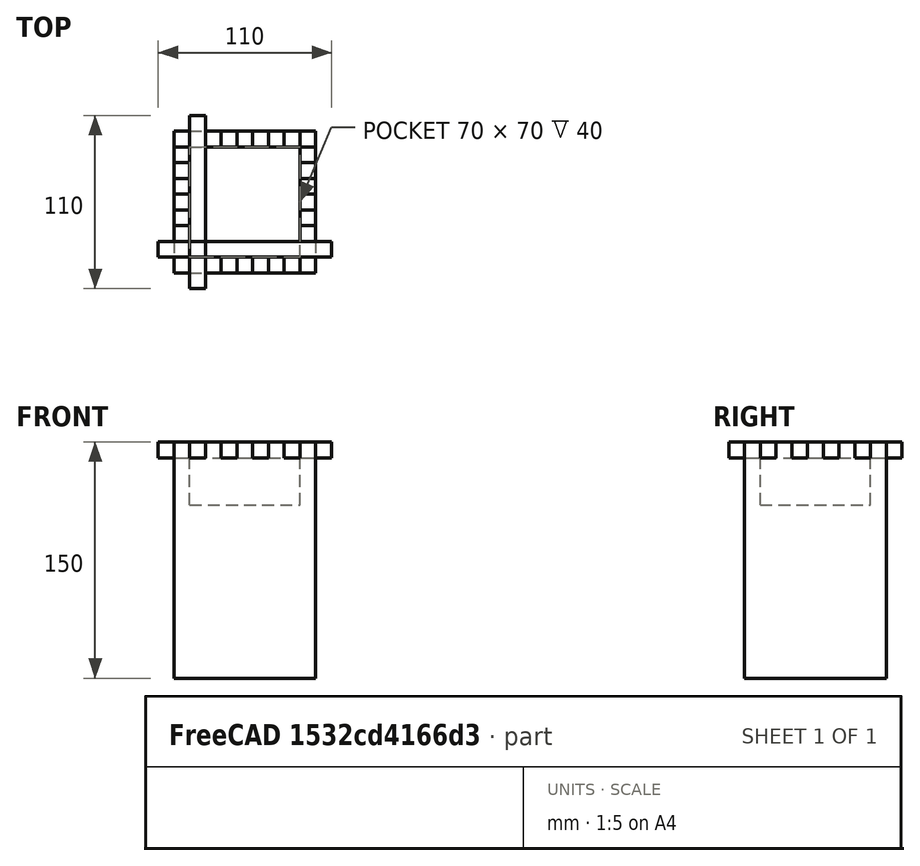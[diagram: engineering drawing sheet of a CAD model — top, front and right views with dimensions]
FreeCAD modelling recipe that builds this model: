
FCSTD DOCUMENT  (FreeCAD 0.21R33694 (Git))
Label: OJT1_T10_R03Castell
License: All rights reserved
LicenseURL: https://en.wikipedia.org/wiki/All_rights_reserved
objects: Part::Box×4, Part::Cut×3, Part::FeaturePython×2, Part::Refine×1
note: 8 computed .brp shape members not serialized (recipe doc carries the construction recipe); baked Part::Feature solids carry a one-line shape summary decoded from their .brp

FEATURE [Part::Box] Box  label="Cub"
  AttacherType = Attacher::AttachEngine3D
  Height = 10
  Length = 10
  Width = 110
FEATURE [Part::FeaturePython] Array  # Draft array (typed FeaturePython)
  AlwaysSyncPlacement = false
  Angle = 360
  ArrayType = 0
  Axis = (0,0,1)
  Base = -> Box
  Center = (0,0,0)
  Count = 4
  ExpandArray = false
  Fuse = false
  IntervalAxis = (0,0,0)
  IntervalX = (20,0,0)
  IntervalY = (0,100,0)
  IntervalZ = (0,0,100)
  NumberCircles = 3
  NumberPolar = 5
  NumberX = 4
  NumberY = 0
  NumberZ = 0
  PlacementList = 4 placements: arithmetic series from (0,0,0) step (20,0,0) to (60,0,0)
  RadialDistance = 50
  ScaleList = (4) [(1,1,1),(1,1,1),(1,1,1),(1,1,1)]
  Symmetry = 1
  TangentialDistance = 25
FEATURE [Part::Box] Box001  label="Cub001"
  AttacherType = Attacher::AttachEngine3D
  Height = 10
  Length = 110
  Placement = pos=(-20,20,0) rot=(0,0,1;0rad)
  Width = 10
  expr: .Placement.Base.x = -20
  expr: .Placement.Base.y = 20
FEATURE [Part::FeaturePython] Array001  # Draft array (typed FeaturePython)
  AlwaysSyncPlacement = false
  Angle = 360
  ArrayType = 0
  Axis = (0,0,1)
  Base = -> Box001
  Center = (0,0,0)
  Count = 4
  ExpandArray = false
  Fuse = false
  IntervalAxis = (0,0,0)
  IntervalX = (100,0,0)
  IntervalY = (0,20,0)
  IntervalZ = (0,0,100)
  NumberCircles = 3
  NumberPolar = 5
  NumberX = 1
  NumberY = 4
  NumberZ = 0
  PlacementList = 4 placements: arithmetic series from (-20,20,0) step (0,20,0) to (-20,80,0)
  RadialDistance = 50
  ScaleList = (4) [(1,1,1),(1,1,1),(1,1,1),(1,1,1)]
  Symmetry = 1
  TangentialDistance = 25
FEATURE [Part::Box] Box002  label="Cub002"
  AttacherType = Attacher::AttachEngine3D
  Height = 150
  Length = 90
  Placement = pos=(-10,10,-140) rot=(0,0,1;0rad)
  Width = 90
  expr: .Placement.Base.x = -10
  expr: .Placement.Base.y = 10
  expr: .Placement.Base.z = -140
FEATURE [Part::Cut] Cut
  Base = -> Box002
  Tool = -> Array
FEATURE [Part::Cut] Cut001
  Base = -> Cut
  Tool = -> Array001
FEATURE [Part::Box] Box003  label="Cub003"
  AttacherType = Attacher::AttachEngine3D
  Height = 50
  Length = 70
  Placement = pos=(0,20,-30) rot=(0,0,1;0rad)
  Width = 70
  expr: .Placement.Base.x = 0
  expr: .Placement.Base.y = 20
  expr: .Placement.Base.z = -30
FEATURE [Part::Cut] Cut002
  Base = -> Cut001
  Tool = -> Box003
FEATURE [Part::Refine] Cut003
  Source = -> Cut002
